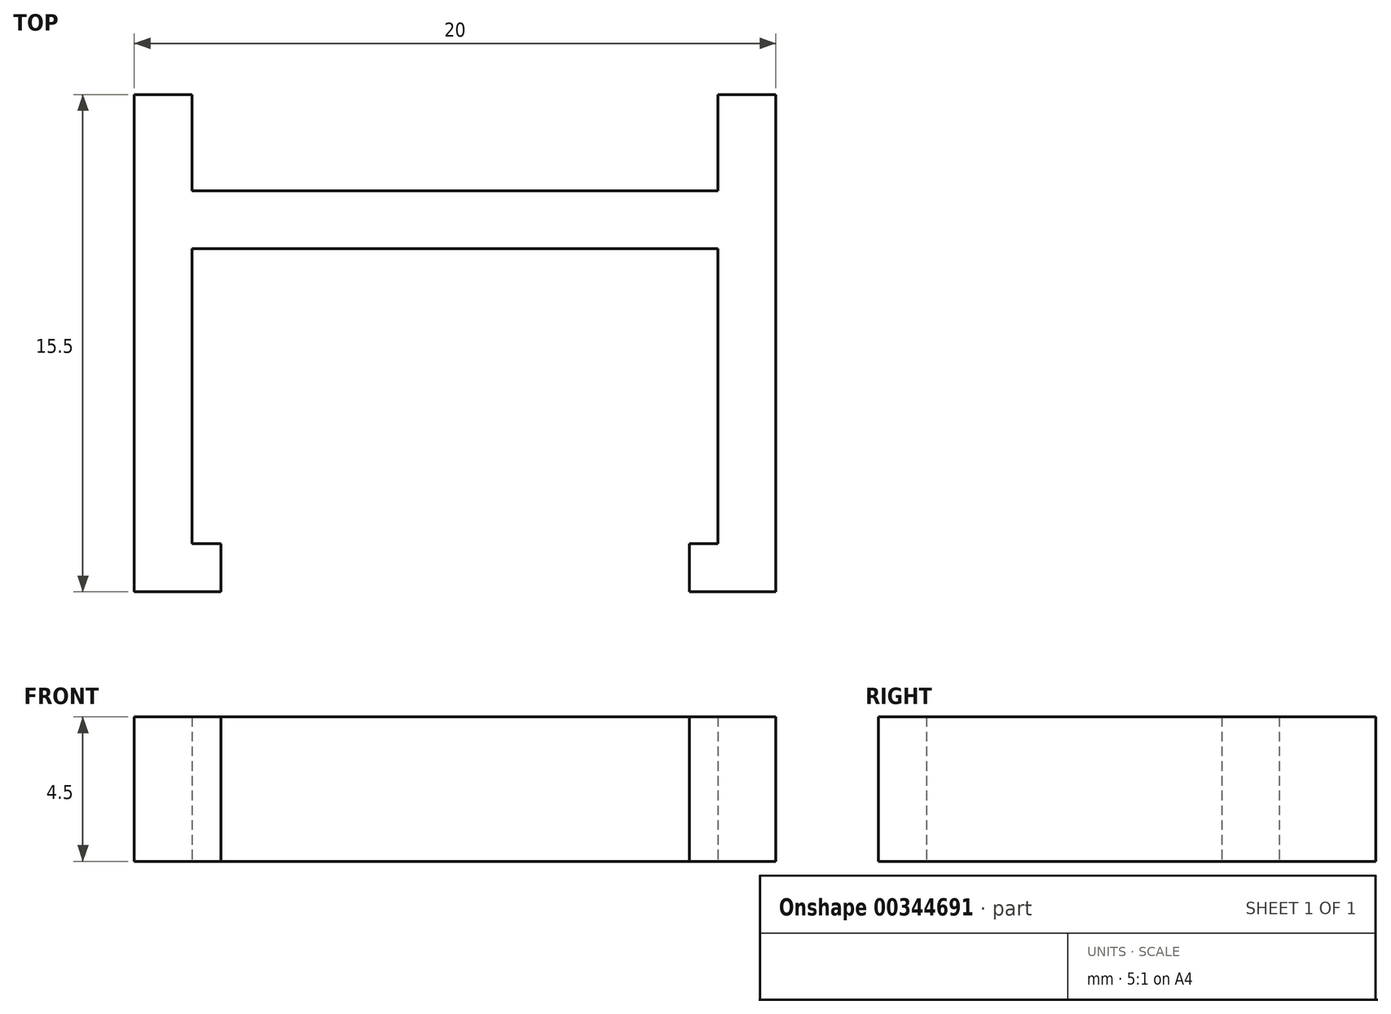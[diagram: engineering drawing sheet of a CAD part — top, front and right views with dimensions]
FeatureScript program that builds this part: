
annotation { "Feature Type Name" : "Feature", "Feature Type Description" : "" }
export const myFeature = defineFeature(function(context is Context, id is Id, definition is map)
    precondition{}
    {
        {
            var Q0;
            Q0=qCreatedBy(makeId("Top.planeOp"),FACE);
            var sketch = newSketch(context, id + "F0", { "sketchPlane" : qUnion([Q0])});
            skLineSegment(sketch, "E0.bottom", {"start": v(-8.2, 0.9) * mm, "end": v(8.2, 0.9) * mm});
            skLineSegment(sketch, "E0.top", {"start": v(-8.2, -0.9) * mm, "end": v(8.2, -0.9) * mm});
            skLineSegment(sketch, "E0.left", {"start": v(-10, 0.9) * mm, "end": v(-10, -0.9) * mm});
            skLineSegment(sketch, "E0.right", {"start": v(10, 0.9) * mm, "end": v(10, -0.9) * mm});
            skPoint(sketch, "E0.middle", {"position": v(0, 0) * mm});
            skLineSegment(sketch, "E1", {"start": v(-10, -0.9) * mm, "end": v(-10, -10.1) * mm});
            skLineSegment(sketch, "E2", {"start": v(-8.2, -10.1) * mm, "end": v(-8.2, -0.9) * mm});
            skLineSegment(sketch, "E3.MirrorCS", {"start": v(8.2, -10.1) * mm, "end": v(8.2, -0.9) * mm});
            skLineSegment(sketch, "E4.MirrorCS", {"start": v(10, -0.9) * mm, "end": v(10, -10.1) * mm});
            skLineSegment(sketch, "E5.bottom", {"start": v(-8.2, -10.1) * mm, "end": v(-7.3, -10.1) * mm});
            skLineSegment(sketch, "E5.top", {"start": v(-10, -11.6) * mm, "end": v(-7.3, -11.6) * mm});
            skLineSegment(sketch, "E5.left", {"start": v(-10, -10.1) * mm, "end": v(-10, -11.6) * mm});
            skLineSegment(sketch, "E5.right", {"start": v(-7.3, -10.1) * mm, "end": v(-7.3, -11.6) * mm});
            skLineSegment(sketch, "E6.MirrorCS", {"start": v(8.2, -10.1) * mm, "end": v(7.3, -10.1) * mm});
            skLineSegment(sketch, "E7.MirrorCS", {"start": v(7.3, -10.1) * mm, "end": v(7.3, -11.6) * mm});
            skLineSegment(sketch, "E8.MirrorCS", {"start": v(10, -11.6) * mm, "end": v(7.3, -11.6) * mm});
            skLineSegment(sketch, "E9.MirrorCS", {"start": v(10, -10.1) * mm, "end": v(10, -11.6) * mm});
            skPoint(sketch, "E10.MirrorCS.end.orphan", {"position": v(8.2, -10.1) * mm});
            skPoint(sketch, "E10.MirrorCS.start.orphan", {"position": v(10, -10.1) * mm});
            skLineSegment(sketch, "E11.top", {"start": v(-10, 3.9) * mm, "end": v(-8.2, 3.9) * mm});
            skLineSegment(sketch, "E11.left", {"start": v(-10, 0.9) * mm, "end": v(-10, 3.9) * mm});
            skLineSegment(sketch, "E11.right", {"start": v(-8.2, 0.9) * mm, "end": v(-8.2, 3.9) * mm});
            skLineSegment(sketch, "E12.MirrorCS", {"start": v(10, 3.9) * mm, "end": v(8.2, 3.9) * mm});
            skLineSegment(sketch, "E13.MirrorCS", {"start": v(10, 0.9) * mm, "end": v(10, 3.9) * mm});
            skLineSegment(sketch, "E14.MirrorCS", {"start": v(8.2, 0.9) * mm, "end": v(8.2, 3.9) * mm});
            skSolve(sketch);
        }
        {
            var Q0;
            Q0=makeQuery(id+"F0.imprint","IMPRINT",FACE,{"disambiguationData":[TD([[makeQuery(id+"F0.imprint","IMPRINT",EDGE,{"derivedFrom":sQuery(id+"F0.wireOp",EDGE,"E0.bottom")}),-1.0]])]});
            extrude(context, id + "F1", {"entities" : qUnion([Q0]), "depth" : 4.5 * mm});
        }
    });
